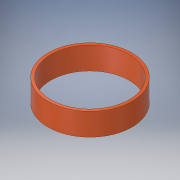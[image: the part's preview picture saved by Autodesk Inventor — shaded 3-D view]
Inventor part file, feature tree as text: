
AUTODESK INVENTOR PART (.ipt)
format: ipt  version: 2017 (Build 210142000, 142)  size: 102,400 bytes
history: native  units: in
note: dims shown in document units (in); Inventor stores cm internally (conversion verified against a paired STEP export)
features: extrude x1, sketch x1
ambient origin geometry x8: Origin, YZ Plane, XZ Plane, XY Plane, X Axis, Y Axis, Z Axis, Center Point
bodies: Solid1 (feature_tree)
feature tree (2):
  extrude  "Extrusion1"  Depth=2.0in
  sketch  "Sketch1"  dims[d0=7.0in d1=7.5in d2=2.0in d3=0.0in]
